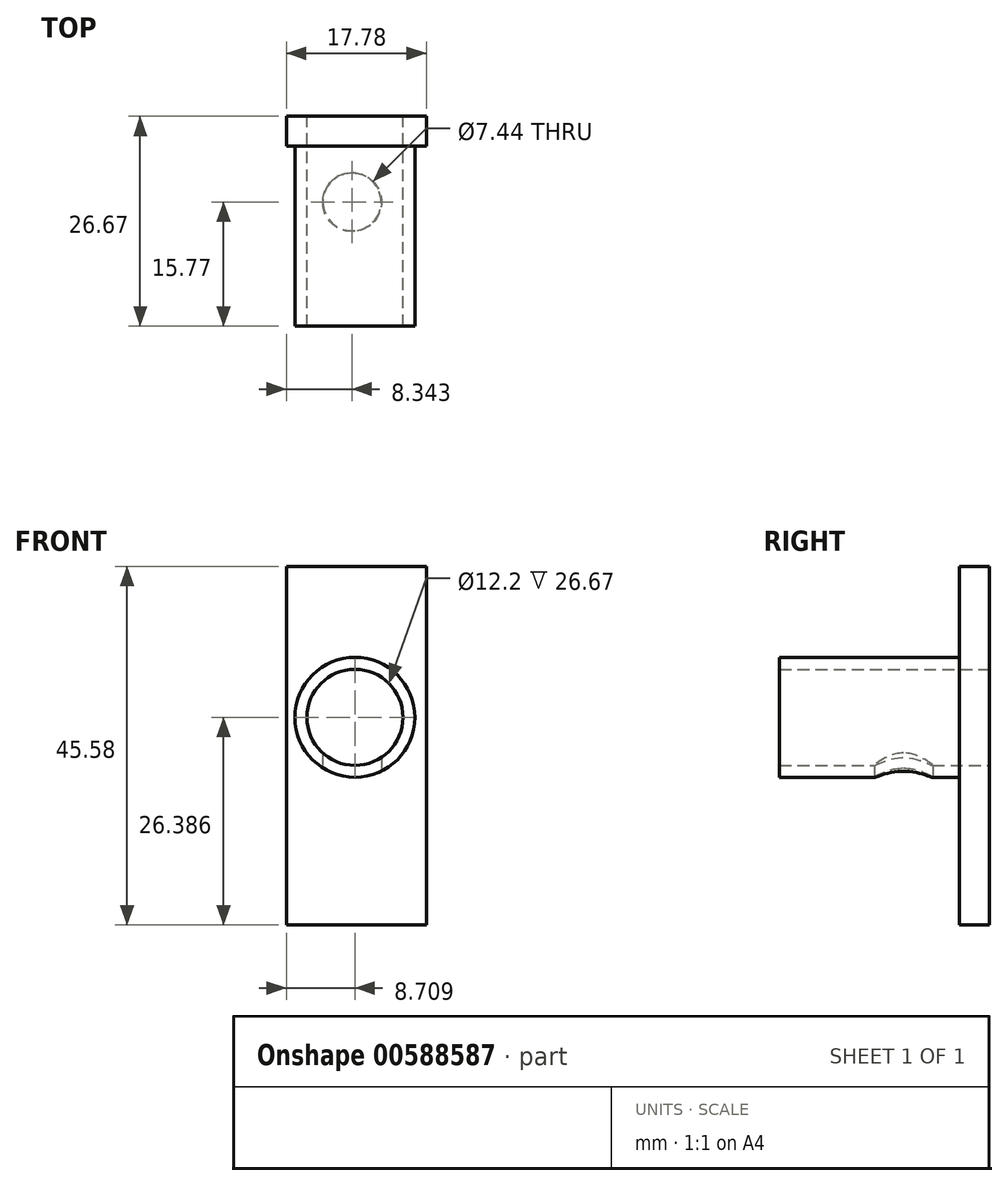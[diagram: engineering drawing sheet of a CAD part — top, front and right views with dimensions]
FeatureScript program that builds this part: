
annotation { "Feature Type Name" : "Feature", "Feature Type Description" : "" }
export const myFeature = defineFeature(function(context is Context, id is Id, definition is map)
    precondition{}
    {
        {
            var Q0;
            Q0=qCreatedBy(makeId("Front.planeOp"),FACE);
            var sketch = newSketch(context, id + "F0", { "sketchPlane" : qUnion([Q0])});
            skCircle(sketch, "E0", {"center": v(-16.96, 18.9) * mm, "radius": 7.62 * mm});
            skSolve(sketch);
        }
        {
            var Q0;
            Q0=makeQuery(id+"F0.imprint","IMPRINT",FACE,{"disambiguationData":[TD([[makeQuery(id+"F0.imprint","IMPRINT",EDGE,{"derivedFrom":sQuery(id+"F0.wireOp",EDGE,"E0")}),1.0]])]});
            extrude(context, id + "F1", {"entities" : qUnion([Q0]), "depth" : 22.86 * mm, "offsetDistance" : 25.4 * mm});
        }
        {
            var Q0;
            Q0=makeQuery(id+"F1.opExtrude","CAP_FACE",FACE,{"disambiguationData":[OSD([sQuery(id+"F0.wireOp",EDGE,"E0")])],"isStart":false});
            var sketch = newSketch(context, id + "F2", { "sketchPlane" : qUnion([Q0])});
            skCircle(sketch, "E1", {"center": v(-16.96, 18.9) * mm, "radius": 5.4 * mm});
            skSolve(sketch);
        }
        {
            var Q0;
            Q0=makeQuery(id+"F2.imprint","IMPRINT",FACE,{"disambiguationData":[TD([[makeQuery(id+"F2.imprint","IMPRINT",EDGE,{"derivedFrom":sQuery(id+"F2.wireOp",EDGE,"E1")}),1.0]])]});
            extrude(context, id + "F3", {"entities" : qUnion([Q0]), "operationType" : NewBodyOperationType.REMOVE, "oppositeDirection" : true, "depth" : 25.4 * mm, "offsetDistance" : 25.4 * mm});
        }
        {
            var Q0;
            Q0=qCreatedBy(makeId("Front.planeOp"),FACE);
            var sketch = newSketch(context, id + "F4", { "sketchPlane" : qUnion([Q0])});
            skLineSegment(sketch, "E2.bottom", {"start": v(-7.89, 38.1) * mm, "end": v(-25.67, 38.1) * mm});
            skLineSegment(sketch, "E2.top", {"start": v(-7.89, -7.5) * mm, "end": v(-25.67, -7.5) * mm});
            skLineSegment(sketch, "E2.left", {"start": v(-7.89, 38.1) * mm, "end": v(-7.89, -7.5) * mm});
            skLineSegment(sketch, "E2.right", {"start": v(-25.67, 38.1) * mm, "end": v(-25.67, -7.5) * mm});
            skSolve(sketch);
        }
        {
            var Q0;
            Q0=makeQuery(id+"F4.imprint","IMPRINT",FACE,{"disambiguationData":[TD([[makeQuery(id+"F4.imprint","IMPRINT",EDGE,{"derivedFrom":sQuery(id+"F4.wireOp",EDGE,"E2.bottom")}),1.0]])]});
            extrude(context, id + "F5", {"entities" : qUnion([Q0]), "operationType" : NewBodyOperationType.ADD, "oppositeDirection" : true, "depth" : 3.8 * mm, "offsetDistance" : 25.4 * mm});
        }
        {
            var Q0;
            Q0=makeQuery(id+"F5.boolean.opBoolean","SPLIT",FACE,{"disambiguationData":[TD([makeQuery(id+"F3.boolean.opBoolean","COPY",FACE,{"derivedFrom":makeQuery(id+"F3.opExtrude","SWEPT_FACE",FACE,{"disambiguationData":[OSD([sQuery(id+"F2.wireOp",EDGE,"E1")])]})})])],"derivedFrom":makeQuery(id+"F5.opExtrude","CAP_FACE",FACE,{"disambiguationData":[OSD([sQuery(id+"F4.wireOp",EDGE,"E2.bottom"),sQuery(id+"F4.wireOp",EDGE,"E2.top"),sQuery(id+"F4.wireOp",EDGE,"E2.left"),sQuery(id+"F4.wireOp",EDGE,"E2.right")])],"isStart":true})});
            extrude(context, id + "F6", {"entities" : qUnion([Q0]), "operationType" : NewBodyOperationType.REMOVE, "oppositeDirection" : true, "depth" : 25.4 * mm, "offsetDistance" : 25.4 * mm});
        }
        {
            var Q0;
            Q0=makeQuery(id+"F5.opExtrude","CAP_FACE",FACE,{"disambiguationData":[OSD([sQuery(id+"F4.wireOp",EDGE,"E2.bottom"),sQuery(id+"F4.wireOp",EDGE,"E2.top"),sQuery(id+"F4.wireOp",EDGE,"E2.left"),sQuery(id+"F4.wireOp",EDGE,"E2.right")])],"isStart":false});
            var sketch = newSketch(context, id + "F7", { "sketchPlane" : qUnion([Q0])});
            skCircle(sketch, "E3", {"center": v(16.96, 18.9) * mm, "radius": 6.1 * mm});
            skSolve(sketch);
        }
        {
            var Q0;
            Q0 = qSketchRegion(id + "F7", true);
            extrude(context, id + "F8", {"entities" : qUnion([Q0]), "operationType" : NewBodyOperationType.REMOVE, "oppositeDirection" : true, "depth" : 25.4 * mm, "offsetDistance" : 25.4 * mm});
        }
        {
            var Q0;
            Q0=qCreatedBy(makeId("Top.planeOp"),FACE);
            var sketch = newSketch(context, id + "F9", { "sketchPlane" : qUnion([Q0])});
            skCircle(sketch, "E4", {"center": v(-17.33, -7.09) * mm, "radius": 3.72 * mm});
            skSolve(sketch);
        }
        {
            var Q0;
            Q0 = qSketchRegion(id + "F9", true);
            extrude(context, id + "F10", {"entities" : qUnion([Q0]), "operationType" : NewBodyOperationType.REMOVE, "depth" : 17.78 * mm, "offsetDistance" : 25.4 * mm});
        }
        {
            var Q0;
            Q0=makeQuery(id+"F8.boolean.opBoolean","COPY",FACE,{"derivedFrom":makeQuery(id+"F8.opExtrude","CAP_FACE",FACE,{"disambiguationData":[OSD([sQuery(id+"F7.wireOp",EDGE,"E3")])],"isStart":false})});
            extrude(context, id + "F11", {"entities" : qUnion([Q0]), "operationType" : NewBodyOperationType.REMOVE, "oppositeDirection" : true, "depth" : 25.4 * mm, "offsetDistance" : 25.4 * mm});
        }
    });
